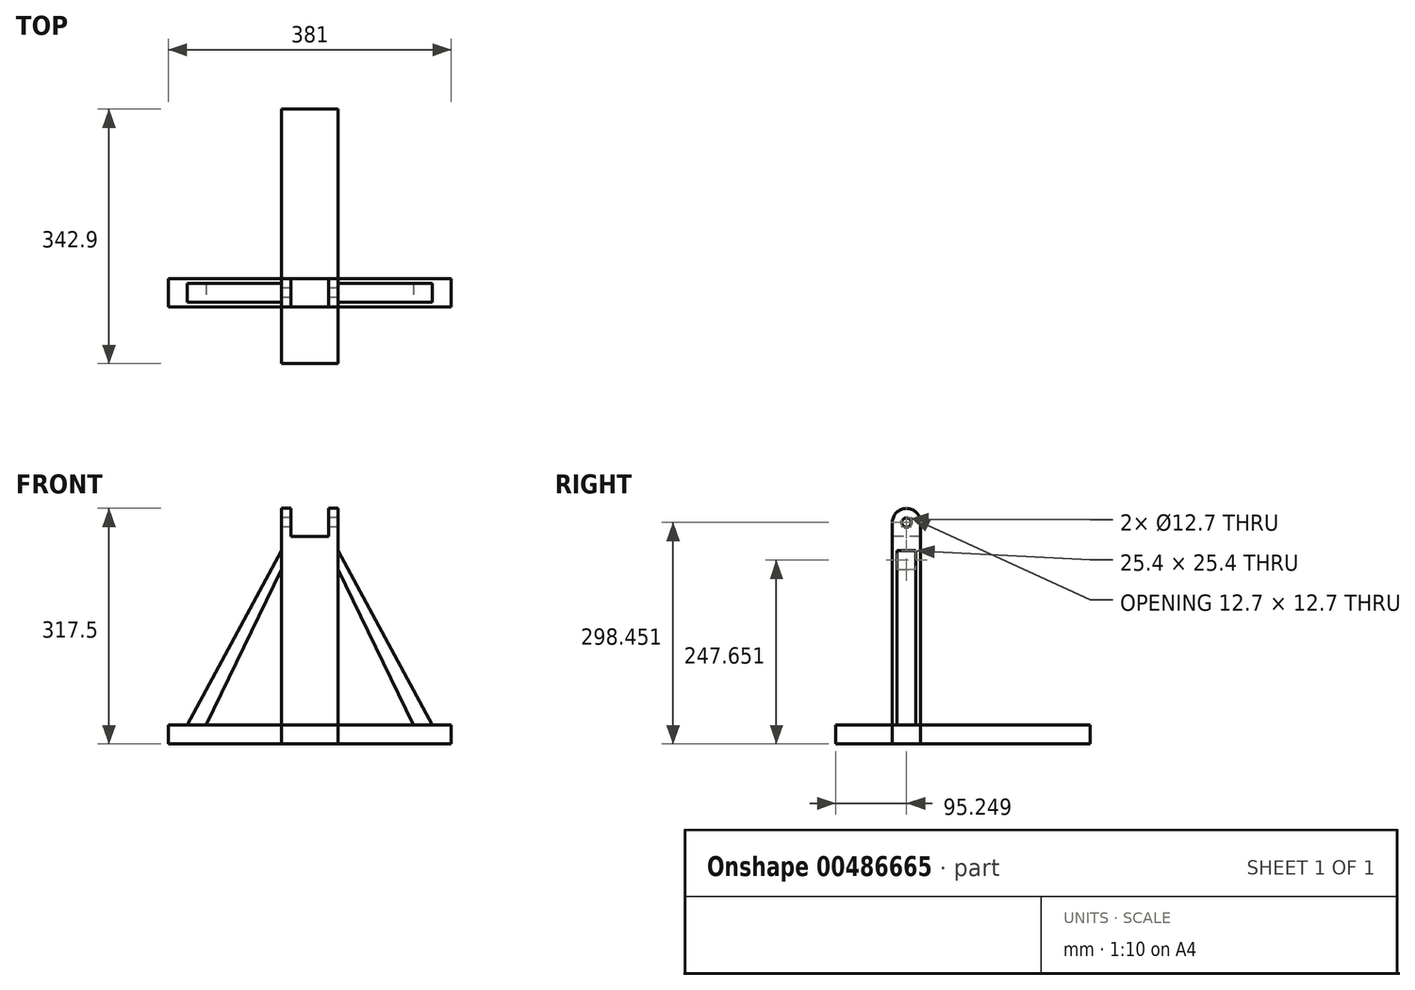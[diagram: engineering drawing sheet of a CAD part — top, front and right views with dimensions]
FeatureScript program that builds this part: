
annotation { "Feature Type Name" : "Feature", "Feature Type Description" : "" }
export const myFeature = defineFeature(function(context is Context, id is Id, definition is map)
    precondition{}
    {
        {
            var Q0;
            Q0=qCreatedBy(makeId("Right.planeOp"),FACE);
            var sketch = newSketch(context, id + "F0", { "sketchPlane" : qUnion([Q0])});
            skLineSegment(sketch, "E0.bottom", {"start": v(-46.72, 234.63) * mm, "end": v(-8.62, 234.63) * mm});
            skLineSegment(sketch, "E0.top", {"start": v(-46.72, -44.77) * mm, "end": v(-8.62, -44.77) * mm});
            skLineSegment(sketch, "E0.left", {"start": v(-46.72, 234.63) * mm, "end": v(-46.72, -44.77) * mm});
            skLineSegment(sketch, "E0.right", {"start": v(-8.62, 234.63) * mm, "end": v(-8.62, -44.77) * mm});
            skLineSegment(sketch, "E1.bottom", {"start": v(-46.72, -44.77) * mm, "end": v(-122.92, -44.77) * mm});
            skLineSegment(sketch, "E1.top", {"start": v(-46.72, -19.37) * mm, "end": v(-122.92, -19.37) * mm});
            skLineSegment(sketch, "E1.left", {"start": v(-46.72, -44.77) * mm, "end": v(-46.72, -19.37) * mm});
            skLineSegment(sketch, "E1.right", {"start": v(-122.92, -44.77) * mm, "end": v(-122.92, -19.37) * mm});
            skLineSegment(sketch, "E2", {"start": v(-46.72, 209.23) * mm, "end": v(-8.62, 209.23) * mm});
            skLineSegment(sketch, "E3.top", {"start": v(-46.72, 253.68) * mm, "end": v(-8.62, 253.68) * mm});
            skLineSegment(sketch, "E3.left", {"start": v(-46.72, 234.63) * mm, "end": v(-46.72, 253.68) * mm});
            skLineSegment(sketch, "E3.right", {"start": v(-8.62, 234.63) * mm, "end": v(-8.62, 253.68) * mm});
            skLineSegment(sketch, "E4.bottom", {"start": v(-8.62, -44.77) * mm, "end": v(219.98, -44.77) * mm});
            skLineSegment(sketch, "E4.top", {"start": v(-8.62, -19.37) * mm, "end": v(219.98, -19.37) * mm});
            skLineSegment(sketch, "E4.left", {"start": v(-8.62, -44.77) * mm, "end": v(-8.62, -19.37) * mm});
            skLineSegment(sketch, "E4.right", {"start": v(219.98, -44.77) * mm, "end": v(219.98, -19.37) * mm});
            skSolve(sketch);
        }
        {
            var Q0;
            {var subQ0=sQuery(id+"F0.wireOp",EDGE,"ZHeRPg9l-sH7m-hoQH-TlfK-Ah8rtcYEaTPo");Q0=makeQuery(id+"F0.imprint","IMPRINT",FACE,{"disambiguationData":[TD([[makeQuery(id+"F0.imprint","IMPRINT",EDGE,{"derivedFrom":subQ0}),1.0]])]});}
            var Q1;
            {var subQ4=sQuery(id+"F0.wireOp",EDGE,"E2");Q1=makeQuery(id+"F0.imprint","IMPRINT",FACE,{"disambiguationData":[TD([[makeQuery(id+"F0.imprint","IMPRINT",EDGE,{"derivedFrom":subQ4}),1.0]])]});}
            var Q2;
            {var subQ2=sQuery(id+"F0.wireOp",EDGE,"ArejXeSJ-AQG4-nWmZ-KchX-uFb6jSuqdiki.bottom");Q2=makeQuery(id+"F0.imprint","IMPRINT",FACE,{"disambiguationData":[TD([[makeQuery(id+"F0.imprint","IMPRINT",EDGE,{"derivedFrom":subQ2}),-1.0]])]});}
            var Q3;
            {var subQ0=sQuery(id+"F0.wireOp",EDGE,"E0.top");Q3=makeQuery(id+"F0.imprint","IMPRINT",FACE,{"disambiguationData":[TD([[makeQuery(id+"F0.imprint","IMPRINT",EDGE,{"derivedFrom":subQ0}),1.0]])]});}
            var Q4;
            Q4=makeQuery(id+"F0.imprint","IMPRINT",FACE,{"disambiguationData":[TD([[makeQuery(id+"F0.imprint","IMPRINT",EDGE,{"derivedFrom":sQuery(id+"F0.wireOp",EDGE,"E1.bottom")}),-1.0]])]});
            var Q5;
            {var subQ0=sQuery(id+"F0.wireOp",EDGE,"ySGlDznE-b9XT-DXzn-5N0W-ZjpT1wRXiVUS");Q5=makeQuery(id+"F0.imprint","IMPRINT",FACE,{"disambiguationData":[TD([[makeQuery(id+"F0.imprint","IMPRINT",EDGE,{"derivedFrom":subQ0}),1.0]])]});}
            var Q6;
            {var subQ0=sQuery(id+"F0.wireOp",EDGE,"E3.left");Q6=makeQuery(id+"F0.imprint","IMPRINT",FACE,{"disambiguationData":[TD([[makeQuery(id+"F0.imprint","IMPRINT",EDGE,{"derivedFrom":subQ0}),-1.0]])]});}
            var Q7;
            {var subQ0=sQuery(id+"F0.wireOp",EDGE,"E3.right");Q7=makeQuery(id+"F0.imprint","IMPRINT",FACE,{"disambiguationData":[TD([[makeQuery(id+"F0.imprint","IMPRINT",EDGE,{"derivedFrom":subQ0}),1.0]])]});}
            var Q8;
            Q8=makeQuery(id+"F0.imprint","IMPRINT",FACE,{"disambiguationData":[TD([[makeQuery(id+"F0.imprint","IMPRINT",EDGE,{"derivedFrom":sQuery(id+"F0.wireOp",EDGE,"E4.bottom")}),1.0]])]});
            extrude(context, id + "F1", {"entities" : qUnion([Q0, Q1, Q2, Q3, Q4, Q5, Q6, Q7, Q8]), "endBound" : BoundingType.SYMMETRIC, "depth" : 76.2 * mm});
        }
        {
            var Q0;
            Q0=makeQuery(id+"F1.opExtrude","SWEPT_FACE",FACE,{"disambiguationData":[OSD([sQuery(id+"F0.wireOp",EDGE,"E3.top")])]});
            var sketch = newSketch(context, id + "F2", { "sketchPlane" : qUnion([Q0])});
            skLineSegment(sketch, "E5", {"start": v(-38.1, -27.67) * mm, "end": v(38.1, -27.67) * mm});
            skSolve(sketch);
        }
        {
            var Q0;
            {var subQ0=sQuery(id+"F2.wireOp",EDGE,"E5");Q0=makeQuery(id+"F2.imprint","IMPRINT",FACE,{"disambiguationData":[TD([[makeQuery(id+"F2.imprint","IMPRINT",EDGE,{"derivedFrom":subQ0}),1.0]])]});}
            var Q1;
            Q1=sQuery(id+"F2.wireOp",EDGE,"E5");
            revolve(context, id + "F3", {"operationType" : NewBodyOperationType.ADD, "entities" : qUnion([Q0]), "axis" : qUnion([Q1]), "revolveType" : RevolveType.FULL});
        }
        {
            var Q0;
            {var subQ0=sQuery(id+"F0.wireOp",EDGE,"E3.top");var subQ1=makeQuery(id+"F1.opExtrude","CAP_EDGE",EDGE,{"disambiguationData":[OSD([subQ0])],"isStart":true});var subQ2=sQuery(id+"F0.wireOp",EDGE,"E3.right");Q0=makeQuery(id+"F3.boolean.opBoolean","MERGE",FACE,{"derivedFrom":[makeQuery(id+"F1.opExtrude","CAP_FACE",FACE,{"disambiguationData":[OSD([sQuery(id+"F0.wireOp",EDGE,"E0.top"),sQuery(id+"F0.wireOp",EDGE,"E0.left"),sQuery(id+"F0.wireOp",EDGE,"E0.right"),sQuery(id+"F0.wireOp",EDGE,"E1.bottom"),sQuery(id+"F0.wireOp",EDGE,"E1.top"),sQuery(id+"F0.wireOp",EDGE,"E1.right"),subQ0,sQuery(id+"F0.wireOp",EDGE,"E3.left"),subQ2])],"isStart":true}),makeQuery(id+"F3.opRevolve","SWEPT_FACE",FACE,{"disambiguationData":[OSD([subQ0]),TDD([makeQuery(id+"F2.imprint","IMPRINT",EDGE,{"disambiguationData":[TD([[makeQuery(id+"F2.imprint","INTERSECT",VERTEX,{"derivedFrom":[subQ1,sQuery(id+"F2.wireOp",EDGE,"E5")]}),-1.0]])],"derivedFrom":subQ1})])]})]});}
            var sketch = newSketch(context, id + "F4", { "sketchPlane" : qUnion([Q0])});
            skCircle(sketch, "E6", {"center": v(27.67, 253.68) * mm, "radius": 6.35 * mm});
            skSolve(sketch);
        }
        {
            var Q0;
            Q0 = qSketchRegion(id + "F4", true);
            extrude(context, id + "F5", {"entities" : qUnion([Q0]), "operationType" : NewBodyOperationType.REMOVE, "oppositeDirection" : true, "depth" : 76.2 * mm});
        }
        {
            var Q0;
            Q0=makeQuery(id+"F1.opExtrude","SWEPT_FACE",FACE,{"disambiguationData":[OSD([sQuery(id+"F0.wireOp",EDGE,"E0.left"),sQuery(id+"F0.wireOp",EDGE,"E3.left")])]});
            var sketch = newSketch(context, id + "F6", { "sketchPlane" : qUnion([Q0])});
            skPoint(sketch, "E7", {"position": v(0, 253.68) * mm});
            skLineSegment(sketch, "E8.bottom", {"start": v(-25.4, 253.68) * mm, "end": v(25.4, 253.68) * mm});
            skLineSegment(sketch, "E8.top", {"start": v(-25.4, 279.08) * mm, "end": v(25.4, 279.08) * mm});
            skLineSegment(sketch, "E8.left", {"start": v(-25.4, 253.68) * mm, "end": v(-25.4, 279.08) * mm});
            skLineSegment(sketch, "E8.right", {"start": v(25.4, 253.68) * mm, "end": v(25.4, 279.08) * mm});
            skPoint(sketch, "E8.middle", {"position": v(0, 266.38) * mm});
            skLineSegment(sketch, "E9.top", {"start": v(-25.4, 234.63) * mm, "end": v(25.4, 234.63) * mm});
            skLineSegment(sketch, "E9.left", {"start": v(-25.4, 253.68) * mm, "end": v(-25.4, 234.63) * mm});
            skLineSegment(sketch, "E9.right", {"start": v(25.4, 253.68) * mm, "end": v(25.4, 234.63) * mm});
            skSolve(sketch);
        }
        {
            var Q0;
            Q0 = qSketchRegion(id + "F6", true);
            extrude(context, id + "F7", {"entities" : qUnion([Q0]), "operationType" : NewBodyOperationType.REMOVE, "oppositeDirection" : true, "depth" : 50.8 * mm});
        }
        {
            var Q0;
            {var subQ0=sQuery(id+"F0.wireOp",EDGE,"E3.top");var subQ1=makeQuery(id+"F1.opExtrude","CAP_EDGE",EDGE,{"disambiguationData":[OSD([subQ0])],"isStart":true});var subQ2=sQuery(id+"F0.wireOp",EDGE,"E3.right");Q0=makeQuery(id+"F3.boolean.opBoolean","MERGE",FACE,{"derivedFrom":[makeQuery(id+"F1.opExtrude","CAP_FACE",FACE,{"disambiguationData":[OSD([sQuery(id+"F0.wireOp",EDGE,"E0.top"),sQuery(id+"F0.wireOp",EDGE,"E0.left"),sQuery(id+"F0.wireOp",EDGE,"E0.right"),sQuery(id+"F0.wireOp",EDGE,"E1.bottom"),sQuery(id+"F0.wireOp",EDGE,"E1.top"),sQuery(id+"F0.wireOp",EDGE,"E1.right"),subQ0,sQuery(id+"F0.wireOp",EDGE,"E3.left"),subQ2,sQuery(id+"F0.wireOp",EDGE,"E4.bottom"),sQuery(id+"F0.wireOp",EDGE,"E4.top"),sQuery(id+"F0.wireOp",EDGE,"E4.right")])],"isStart":true}),makeQuery(id+"F3.opRevolve","SWEPT_FACE",FACE,{"disambiguationData":[OSD([subQ0]),TDD([makeQuery(id+"F2.imprint","IMPRINT",EDGE,{"disambiguationData":[TD([[makeQuery(id+"F2.imprint","INTERSECT",VERTEX,{"derivedFrom":[subQ1,sQuery(id+"F2.wireOp",EDGE,"E5")]}),-1.0]])],"derivedFrom":subQ1})])]})]});}
            var sketch = newSketch(context, id + "F8", { "sketchPlane" : qUnion([Q0])});
            skLineSegment(sketch, "E10.bottom", {"start": v(8.62, -19.37) * mm, "end": v(46.72, -19.37) * mm});
            skLineSegment(sketch, "E10.top", {"start": v(8.62, -44.77) * mm, "end": v(46.72, -44.77) * mm});
            skLineSegment(sketch, "E10.left", {"start": v(8.62, -19.37) * mm, "end": v(8.62, -44.77) * mm});
            skLineSegment(sketch, "E10.right", {"start": v(46.72, -19.37) * mm, "end": v(46.72, -44.77) * mm});
            skSolve(sketch);
        }
        {
            var Q0;
            Q0 = qSketchRegion(id + "F8", true);
            extrude(context, id + "F9", {"entities" : qUnion([Q0]), "operationType" : NewBodyOperationType.ADD, "depth" : 152.4 * mm});
        }
        {
            var Q0;
            {var subQ0=sQuery(id+"F0.wireOp",EDGE,"E3.top");var subQ1=makeQuery(id+"F1.opExtrude","CAP_EDGE",EDGE,{"disambiguationData":[OSD([subQ0])],"isStart":false});var subQ2=sQuery(id+"F0.wireOp",EDGE,"E3.right");Q0=makeQuery(id+"F3.boolean.opBoolean","MERGE",FACE,{"derivedFrom":[makeQuery(id+"F1.opExtrude","CAP_FACE",FACE,{"disambiguationData":[OSD([sQuery(id+"F0.wireOp",EDGE,"E0.top"),sQuery(id+"F0.wireOp",EDGE,"E0.left"),sQuery(id+"F0.wireOp",EDGE,"E0.right"),sQuery(id+"F0.wireOp",EDGE,"E1.bottom"),sQuery(id+"F0.wireOp",EDGE,"E1.top"),sQuery(id+"F0.wireOp",EDGE,"E1.right"),subQ0,sQuery(id+"F0.wireOp",EDGE,"E3.left"),subQ2,sQuery(id+"F0.wireOp",EDGE,"E4.bottom"),sQuery(id+"F0.wireOp",EDGE,"E4.top"),sQuery(id+"F0.wireOp",EDGE,"E4.right")])],"isStart":false}),makeQuery(id+"F3.opRevolve","SWEPT_FACE",FACE,{"disambiguationData":[OSD([subQ0]),TDD([makeQuery(id+"F2.imprint","IMPRINT",EDGE,{"disambiguationData":[TD([[makeQuery(id+"F2.imprint","INTERSECT",VERTEX,{"derivedFrom":[subQ1,sQuery(id+"F2.wireOp",EDGE,"E5")]}),-1.0]])],"derivedFrom":subQ1})])]})]});}
            var sketch = newSketch(context, id + "F10", { "sketchPlane" : qUnion([Q0])});
            skLineSegment(sketch, "E11.bottom", {"start": v(-46.72, -19.37) * mm, "end": v(-8.62, -19.37) * mm});
            skLineSegment(sketch, "E11.top", {"start": v(-46.72, -44.77) * mm, "end": v(-8.62, -44.77) * mm});
            skLineSegment(sketch, "E11.left", {"start": v(-46.72, -19.37) * mm, "end": v(-46.72, -44.77) * mm});
            skLineSegment(sketch, "E11.right", {"start": v(-8.62, -19.37) * mm, "end": v(-8.62, -44.77) * mm});
            skSolve(sketch);
        }
        {
            var Q0;
            Q0 = qSketchRegion(id + "F10", true);
            extrude(context, id + "F11", {"entities" : qUnion([Q0]), "operationType" : NewBodyOperationType.ADD, "depth" : 152.4 * mm});
        }
        {
            var Q0;
            {var subQ0=sQuery(id+"F0.wireOp",EDGE,"E3.top");var subQ1=makeQuery(id+"F1.opExtrude","CAP_EDGE",EDGE,{"disambiguationData":[OSD([subQ0])],"isStart":true});var subQ2=sQuery(id+"F0.wireOp",EDGE,"E3.right");var subQ3=makeQuery(id+"F3.opRevolve","SWEPT_FACE",FACE,{"disambiguationData":[OSD([subQ0]),TDD([makeQuery(id+"F2.imprint","IMPRINT",EDGE,{"disambiguationData":[TD([[makeQuery(id+"F2.imprint","INTERSECT",VERTEX,{"derivedFrom":[subQ1,sQuery(id+"F2.wireOp",EDGE,"E5")]}),-1.0]])],"derivedFrom":subQ1})])]});var subQ4=sQuery(id+"F0.wireOp",EDGE,"E1.top");var subQ5=sQuery(id+"F0.wireOp",EDGE,"E0.right");var subQ6=sQuery(id+"F0.wireOp",EDGE,"E4.top");var subQ7=sQuery(id+"F0.wireOp",EDGE,"E3.left");var subQ8=sQuery(id+"F0.wireOp",EDGE,"E0.left");var subQ9=makeQuery(id+"F1.opExtrude","CAP_FACE",FACE,{"disambiguationData":[OSD([sQuery(id+"F0.wireOp",EDGE,"E0.top"),subQ8,subQ5,sQuery(id+"F0.wireOp",EDGE,"E1.bottom"),subQ4,sQuery(id+"F0.wireOp",EDGE,"E1.right"),subQ0,subQ7,subQ2,sQuery(id+"F0.wireOp",EDGE,"E4.bottom"),subQ6,sQuery(id+"F0.wireOp",EDGE,"E4.right")])],"isStart":true});Q0=makeQuery(id+"F9.boolean.opBoolean","SPLIT",FACE,{"disambiguationData":[TD([makeQuery(id+"F5.boolean.opBoolean","COPY",FACE,{"derivedFrom":makeQuery(id+"F5.opExtrude","SWEPT_FACE",FACE,{"disambiguationData":[OSD([sQuery(id+"F4.wireOp",EDGE,"E6")])]})})])],"derivedFrom":makeQuery(id+"F3.boolean.opBoolean","MERGE",FACE,{"derivedFrom":[subQ9,subQ3]})});}
            var sketch = newSketch(context, id + "F12", { "sketchPlane" : qUnion([Q0])});
            skLineSegment(sketch, "E12.bottom", {"start": v(14.97, 215.58) * mm, "end": v(40.37, 215.58) * mm});
            skLineSegment(sketch, "E12.top", {"start": v(14.97, 190.18) * mm, "end": v(40.37, 190.18) * mm});
            skLineSegment(sketch, "E12.left", {"start": v(14.97, 215.58) * mm, "end": v(14.97, 190.18) * mm});
            skLineSegment(sketch, "E12.right", {"start": v(40.37, 215.58) * mm, "end": v(40.37, 190.18) * mm});
            skPoint(sketch, "E12.middle", {"position": v(27.67, 202.88) * mm});
            skSolve(sketch);
        }
        {
            var Q0;
            Q0=makeQuery(id+"F9.opExtrude","SWEPT_FACE",FACE,{"disambiguationData":[OSD([sQuery(id+"F8.wireOp",EDGE,"E10.bottom")])]});
            var sketch = newSketch(context, id + "F13", { "sketchPlane" : qUnion([Q0])});
            skLineSegment(sketch, "E13.bottom", {"start": v(-165.1, -14.97) * mm, "end": v(-139.7, -14.97) * mm});
            skLineSegment(sketch, "E13.top", {"start": v(-165.1, -40.37) * mm, "end": v(-139.7, -40.37) * mm});
            skLineSegment(sketch, "E13.left", {"start": v(-165.1, -14.97) * mm, "end": v(-165.1, -40.37) * mm});
            skLineSegment(sketch, "E13.right", {"start": v(-139.7, -14.97) * mm, "end": v(-139.7, -40.37) * mm});
            skPoint(sketch, "E13.middle", {"position": v(-152.4, -27.67) * mm});
            skSolve(sketch);
        }
        {
            var Q1;
            Q1=makeQuery(id+"F13.imprint","IMPRINT",FACE,{"disambiguationData":[TD([[makeQuery(id+"F13.imprint","IMPRINT",EDGE,{"derivedFrom":sQuery(id+"F13.wireOp",EDGE,"E13.bottom")}),-1.0]])]});
            var Q2;
            Q2=makeQuery(id+"F12.imprint","IMPRINT",FACE,{"disambiguationData":[TD([[makeQuery(id+"F12.imprint","IMPRINT",EDGE,{"derivedFrom":sQuery(id+"F12.wireOp",EDGE,"E12.bottom")}),-1.0]])]});
            loft(context, id + "F14", {"operationType" : NewBodyOperationType.ADD, "sheetProfilesArray" : [{ "sheetProfileEntities" : qUnion([Q1]) }, { "sheetProfileEntities" : qUnion([Q2]) }]});
        }
        {
            var Q0;
            {var subQ0=sQuery(id+"F0.wireOp",EDGE,"E4.top");var subQ1=sQuery(id+"F0.wireOp",EDGE,"E3.right");var subQ2=sQuery(id+"F0.wireOp",EDGE,"E3.top");var subQ3=sQuery(id+"F0.wireOp",EDGE,"E0.right");var subQ4=sQuery(id+"F0.wireOp",EDGE,"E3.left");var subQ5=sQuery(id+"F0.wireOp",EDGE,"E1.top");var subQ6=sQuery(id+"F0.wireOp",EDGE,"E0.left");var subQ7=makeQuery(id+"F1.opExtrude","CAP_FACE",FACE,{"disambiguationData":[OSD([sQuery(id+"F0.wireOp",EDGE,"E0.top"),subQ6,subQ3,sQuery(id+"F0.wireOp",EDGE,"E1.bottom"),subQ5,sQuery(id+"F0.wireOp",EDGE,"E1.right"),subQ2,subQ4,subQ1,sQuery(id+"F0.wireOp",EDGE,"E4.bottom"),subQ0,sQuery(id+"F0.wireOp",EDGE,"E4.right")])],"isStart":false});var subQ8=makeQuery(id+"F1.opExtrude","CAP_EDGE",EDGE,{"disambiguationData":[OSD([subQ2])],"isStart":false});var subQ9=makeQuery(id+"F3.opRevolve","SWEPT_FACE",FACE,{"disambiguationData":[OSD([subQ2]),TDD([makeQuery(id+"F2.imprint","IMPRINT",EDGE,{"disambiguationData":[TD([[makeQuery(id+"F2.imprint","INTERSECT",VERTEX,{"derivedFrom":[subQ8,sQuery(id+"F2.wireOp",EDGE,"E5")]}),-1.0]])],"derivedFrom":subQ8})])]});Q0=makeQuery(id+"F11.boolean.opBoolean","SPLIT",FACE,{"disambiguationData":[TD([makeQuery(id+"F5.boolean.opBoolean","COPY",FACE,{"derivedFrom":makeQuery(id+"F5.opExtrude","SWEPT_FACE",FACE,{"disambiguationData":[OSD([sQuery(id+"F4.wireOp",EDGE,"E6")])]})})])],"derivedFrom":makeQuery(id+"F3.boolean.opBoolean","MERGE",FACE,{"derivedFrom":[subQ7,subQ9]})});}
            var sketch = newSketch(context, id + "F15", { "sketchPlane" : qUnion([Q0])});
            skLineSegment(sketch, "E14.bottom", {"start": v(-40.37, 215.58) * mm, "end": v(-14.97, 215.58) * mm});
            skLineSegment(sketch, "E14.top", {"start": v(-40.37, 190.18) * mm, "end": v(-14.97, 190.18) * mm});
            skLineSegment(sketch, "E14.left", {"start": v(-40.37, 215.58) * mm, "end": v(-40.37, 190.18) * mm});
            skLineSegment(sketch, "E14.right", {"start": v(-14.97, 215.58) * mm, "end": v(-14.97, 190.18) * mm});
            skPoint(sketch, "E14.middle", {"position": v(-27.67, 202.88) * mm});
            skSolve(sketch);
        }
        {
            var Q0;
            Q0=makeQuery(id+"F11.opExtrude","SWEPT_FACE",FACE,{"disambiguationData":[OSD([sQuery(id+"F10.wireOp",EDGE,"E11.bottom")])]});
            var sketch = newSketch(context, id + "F16", { "sketchPlane" : qUnion([Q0])});
            skLineSegment(sketch, "E15.bottom", {"start": v(165.1, -14.97) * mm, "end": v(139.7, -14.97) * mm});
            skLineSegment(sketch, "E15.top", {"start": v(165.1, -40.37) * mm, "end": v(139.7, -40.37) * mm});
            skLineSegment(sketch, "E15.left", {"start": v(165.1, -14.97) * mm, "end": v(165.1, -40.37) * mm});
            skLineSegment(sketch, "E15.right", {"start": v(139.7, -14.97) * mm, "end": v(139.7, -40.37) * mm});
            skPoint(sketch, "E15.middle", {"position": v(152.4, -27.67) * mm});
            skSolve(sketch);
        }
        {
            var Q1;
            Q1=makeQuery(id+"F16.imprint","IMPRINT",FACE,{"disambiguationData":[TD([[makeQuery(id+"F16.imprint","IMPRINT",EDGE,{"derivedFrom":sQuery(id+"F16.wireOp",EDGE,"E15.bottom")}),1.0]])]});
            var Q2;
            Q2=makeQuery(id+"F15.imprint","IMPRINT",FACE,{"disambiguationData":[TD([[makeQuery(id+"F15.imprint","IMPRINT",EDGE,{"derivedFrom":sQuery(id+"F15.wireOp",EDGE,"E14.bottom")}),-1.0]])]});
            loft(context, id + "F17", {"operationType" : NewBodyOperationType.ADD, "sheetProfilesArray" : [{ "sheetProfileEntities" : qUnion([Q1]) }, { "sheetProfileEntities" : qUnion([Q2]) }]});
        }
    });
